FCSTD DOCUMENT  (FreeCAD 0.15R4671 (Git))
Label: 2HEPanel_AlbrechtAE4200
License: All rights reserved
LicenseURL: http://en.wikipedia.org/wiki/All_rights_reserved
objects: Sketcher::SketchObject×1
note: 1 computed .brp shape members not serialized (recipe doc carries the construction recipe); baked Part::Feature solids carry a one-line shape summary decoded from their .brp

FEATURE [Sketcher::SketchObject] Sketch
  sketch-geometry (22):
    g0: LineSegment StartX=0 StartY=0 StartZ=0 EndX=180.083 EndY=0 EndZ=0
    g1: LineSegment StartX=180.083 StartY=0 StartZ=0 EndX=180.083 EndY=60.0749 EndZ=0
    g2: LineSegment StartX=180.083 StartY=60.0749 StartZ=0 EndX=0 EndY=60.0749 EndZ=0
    g3: LineSegment StartX=0 StartY=60.0749 StartZ=0 EndX=0 EndY=0 EndZ=0
    g4: Circle CenterX=3.70761 CenterY=56.5448 CenterZ=0 NormalX=0 NormalY=0 NormalZ=1 Radius=2.16509
    g5: Circle CenterX=3.52213 CenterY=3.96001 CenterZ=0 NormalX=0 NormalY=0 NormalZ=1 Radius=2.1986
    g6: Circle CenterX=176.579 CenterY=56.4521 CenterZ=0 NormalX=0 NormalY=0 NormalZ=1 Radius=2.22582
    g7: Circle CenterX=176.764 CenterY=3.77452 CenterZ=0 NormalX=0 NormalY=0 NormalZ=1 Radius=2.1631
    g8: Circle CenterX=23.3563 CenterY=9.89327 CenterZ=0 NormalX=0 NormalY=0 NormalZ=1 Radius=7.60825
    g9: LineSegment StartX=25.6749 StartY=55.8934 StartZ=0 EndX=154.03 EndY=55.8934 EndZ=0
    g10: LineSegment StartX=154.03 StartY=55.8934 StartZ=0 EndX=154.03 EndY=22.228 EndZ=0
    g11: LineSegment StartX=154.03 StartY=22.228 StartZ=0 EndX=25.6749 EndY=22.228 EndZ=0
    g12: LineSegment StartX=25.6749 StartY=22.228 StartZ=0 EndX=25.6749 EndY=55.8934 EndZ=0
    g13: Circle CenterX=156.163 CenterY=9.98601 CenterZ=0 NormalX=0 NormalY=0 NormalZ=1 Radius=7.51156
    g14: LineSegment StartX=57.6709 StartY=19.7239 StartZ=0 EndX=122.961 EndY=19.7239 EndZ=0
    g15: LineSegment StartX=122.961 StartY=19.7239 StartZ=0 EndX=122.961 EndY=2.19567 EndZ=0
    g16: LineSegment StartX=122.961 StartY=2.19567 StartZ=0 EndX=57.6709 EndY=2.19567 EndZ=0
    g17: LineSegment StartX=57.6709 StartY=2.19567 StartZ=0 EndX=57.6709 EndY=19.7239 EndZ=0
    g18: Circle CenterX=39.9572 CenterY=5.44164 CenterZ=0 NormalX=0 NormalY=0 NormalZ=1 Radius=2.5785
    g19: Circle CenterX=50.0661 CenterY=5.53438 CenterZ=0 NormalX=0 NormalY=0 NormalZ=1 Radius=2.59844
    g20: Circle CenterX=129.917 CenterY=5.62712 CenterZ=0 NormalX=0 NormalY=0 NormalZ=1 Radius=2.62477
    g21: Circle CenterX=139.84 CenterY=5.62712 CenterZ=0 NormalX=0 NormalY=0 NormalZ=1 Radius=2.62478
  constraints (25):
    c: Coincident(g0,g1)
    c: Coincident(g1,g2)
    c: Coincident(g2,g3)
    c: Coincident(g3,g0)
    c: Horizontal(g0)
    c: Horizontal(g2)
    c: Vertical(g1)
    c: Vertical(g3)
    c: Coincident(g0,g-1)
    c: Coincident(g9,g10)
    c: Coincident(g10,g11)
    c: Coincident(g11,g12)
    c: Coincident(g12,g9)
    c: Horizontal(g9)
    c: Horizontal(g11)
    c: Vertical(g10)
    c: Vertical(g12)
    c: Coincident(g14,g15)
    c: Coincident(g15,g16)
    c: Coincident(g16,g17)
    c: Coincident(g17,g14)
    c: Horizontal(g14)
    c: Horizontal(g16)
    c: Vertical(g15)
    c: Vertical(g17)
